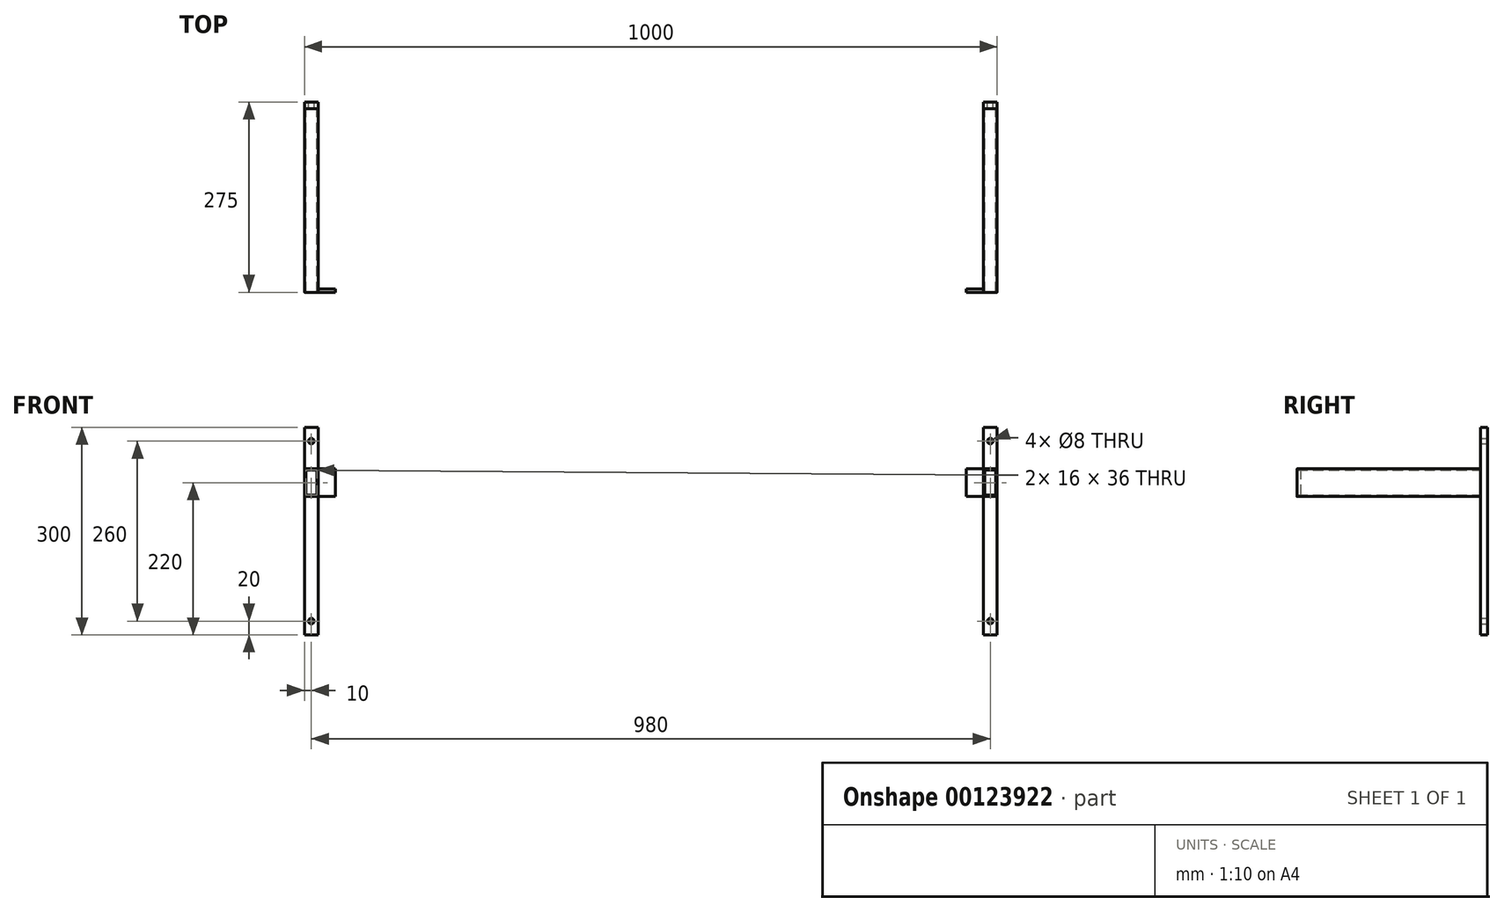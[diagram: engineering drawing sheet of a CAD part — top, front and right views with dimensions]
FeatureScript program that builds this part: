
annotation { "Feature Type Name" : "Feature", "Feature Type Description" : "" }
export const myFeature = defineFeature(function(context is Context, id is Id, definition is map)
    precondition{}
    {
        {
            var Q0;
            Q0=qCreatedBy(makeId("Front.planeOp"),FACE);
            var sketch = newSketch(context, id + "F0", { "sketchPlane" : qUnion([Q0])});
            skLineSegment(sketch, "E0.bottom", {"start": v(10, -150) * mm, "end": v(-10, -150) * mm});
            skLineSegment(sketch, "E0.top", {"start": v(10, 150) * mm, "end": v(-10, 150) * mm});
            skLineSegment(sketch, "E0.left", {"start": v(10, -150) * mm, "end": v(10, 150) * mm});
            skLineSegment(sketch, "E0.right", {"start": v(-10, -150) * mm, "end": v(-10, 150) * mm});
            skPoint(sketch, "E0.middle", {"position": v(0, 0) * mm});
            skLineSegment(sketch, "E1", {"start": v(0, 150) * mm, "end": v(0, -150) * mm, "construction": true});
            skCircle(sketch, "E2", {"center": v(0, 130) * mm, "radius": 4 * mm});
            skCircle(sketch, "E3", {"center": v(0, -130) * mm, "radius": 4 * mm});
            skSolve(sketch);
        }
        {
            var Q0;
            Q0 = qSketchRegion(id + "F0", true);
            extrude(context, id + "F1", {"entities" : qUnion([Q0]), "depth" : 10 * mm});
        }
        {
            var Q0;
            Q0=makeQuery(id+"F1.opExtrude","CAP_FACE",FACE,{"disambiguationData":[OSD([sQuery(id+"F0.wireOp",EDGE,"E0.bottom"),sQuery(id+"F0.wireOp",EDGE,"E0.top"),sQuery(id+"F0.wireOp",EDGE,"E0.left"),sQuery(id+"F0.wireOp",EDGE,"E0.right")])],"isStart":false});
            var sketch = newSketch(context, id + "F2", { "sketchPlane" : qUnion([Q0])});
            skLineSegment(sketch, "E4.bottom", {"start": v(-8, 90) * mm, "end": v(8, 90) * mm});
            skLineSegment(sketch, "E4.top", {"start": v(-8, 50) * mm, "end": v(8, 50) * mm});
            skLineSegment(sketch, "E4.left", {"start": v(-10, 88) * mm, "end": v(-10, 52) * mm});
            skLineSegment(sketch, "E4.right", {"start": v(10, 88) * mm, "end": v(10, 52) * mm});
            skPoint(sketch, "E5.visualSharp", {"position": v(-10, 90) * mm});
            skArc(sketch, "E5.filletArc", {"start": v(-8, 90) * mm, "mid": v(-9.41, 89.41) * mm, "end": v(-10, 88) * mm});
            skPoint(sketch, "E6.visualSharp", {"position": v(10, 90) * mm});
            skArc(sketch, "E6.filletArc", {"start": v(10, 88) * mm, "mid": v(9.41, 89.41) * mm, "end": v(8, 90) * mm});
            skPoint(sketch, "E7.visualSharp", {"position": v(10, 50) * mm});
            skArc(sketch, "E7.filletArc", {"start": v(8, 50) * mm, "mid": v(9.41, 50.59) * mm, "end": v(10, 52) * mm});
            skPoint(sketch, "E8.visualSharp", {"position": v(-10, 50) * mm});
            skArc(sketch, "E8.filletArc", {"start": v(-10, 52) * mm, "mid": v(-9.41, 50.59) * mm, "end": v(-8, 50) * mm});
            skLineSegment(sketch, "E9", {"start": v(0, 90) * mm, "end": v(0, 50) * mm});
            skLineSegment(sketch, "E10.bottom", {"start": v(8, 52) * mm, "end": v(-8, 52) * mm});
            skLineSegment(sketch, "E10.top", {"start": v(8, 88) * mm, "end": v(-8, 88) * mm});
            skLineSegment(sketch, "E10.left", {"start": v(8, 52) * mm, "end": v(8, 88) * mm});
            skLineSegment(sketch, "E10.right", {"start": v(-8, 52) * mm, "end": v(-8, 88) * mm});
            skPoint(sketch, "E10.middle", {"position": v(0, 70) * mm});
            skSolve(sketch);
        }
        {
            var Q0;
            Q0 = qSketchRegion(id + "F2", true);
            extrude(context, id + "F3", {"entities" : qUnion([Q0]), "depth" : (300 - 25 - 10) * mm});
        }
        {
            var Q0;
            Q0=qCreatedBy(makeId("Right.planeOp"),FACE);
            cPlane(context, id + "F4", {"entities" : qUnion([Q0]), "cplaneType" : CPlaneType.OFFSET, "offset" : 10 * mm, "oppositeDirection" : true, "width" : 150 * mm, "height" : 150 * mm});
        }
        {
            var Q0;
            Q0=qCreatedBy(id+"F4.planeOp",FACE);
            cPlane(context, id + "F5", {"entities" : qUnion([Q0]), "cplaneType" : CPlaneType.OFFSET, "offset" : 500 * mm, "width" : 150 * mm, "height" : 150 * mm});
        }
        {
            var Q0;
            Q0=makeQuery(id+"F3.boolean.opBoolean","MERGE",FACE,{"derivedFrom":[makeQuery(id+"F1.opExtrude","SWEPT_FACE",FACE,{"disambiguationData":[OSD([sQuery(id+"F0.wireOp",EDGE,"E0.left")])]}),makeQuery(id+"F3.opExtrude","SWEPT_FACE",FACE,{"disambiguationData":[OSD([sQuery(id+"F2.wireOp",EDGE,"E4.right")])]})]});
            var sketch = newSketch(context, id + "F6", { "sketchPlane" : qUnion([Q0])});
            skLineSegment(sketch, "E11", {"start": v(-275, 88) * mm, "end": v(-275, 52) * mm, "construction": true});
            skLineSegment(sketch, "E12.bottom", {"start": v(-275, 90) * mm, "end": v(-270, 90) * mm});
            skLineSegment(sketch, "E12.top", {"start": v(-275, 50) * mm, "end": v(-270, 50) * mm});
            skLineSegment(sketch, "E12.left", {"start": v(-275, 90) * mm, "end": v(-275, 50) * mm});
            skLineSegment(sketch, "E12.right", {"start": v(-270, 90) * mm, "end": v(-270, 50) * mm});
            skSolve(sketch);
        }
        {
            var Q0;
            Q0 = qSketchRegion(id + "F6", true);
            extrude(context, id + "F7", {"entities" : qUnion([Q0]), "depth" : 25 * mm});
        }
        {
            var Q0;
            Q0=makeQuery(id+"F1.opExtrude","SWEPT_BODY",BODY,{"disambiguationData":[OSD([sQuery(id+"F0.wireOp",EDGE,"E0.bottom"),sQuery(id+"F0.wireOp",EDGE,"E0.top"),sQuery(id+"F0.wireOp",EDGE,"E0.left"),sQuery(id+"F0.wireOp",EDGE,"E0.right")])]});
            var Q1;
            Q1=makeQuery(id+"F3.opExtrude","SWEPT_BODY",BODY,{"disambiguationData":[OSD([sQuery(id+"F2.wireOp",EDGE,"E4.bottom"),sQuery(id+"F2.wireOp",EDGE,"E4.top"),sQuery(id+"F2.wireOp",EDGE,"E4.left"),sQuery(id+"F2.wireOp",EDGE,"E4.right"),sQuery(id+"F2.wireOp",EDGE,"E5.filletArc"),sQuery(id+"F2.wireOp",EDGE,"E6.filletArc"),sQuery(id+"F2.wireOp",EDGE,"E7.filletArc"),sQuery(id+"F2.wireOp",EDGE,"E8.filletArc"),sQuery(id+"F2.wireOp",EDGE,"E10.bottom"),sQuery(id+"F2.wireOp",EDGE,"E10.top"),sQuery(id+"F2.wireOp",EDGE,"E10.left"),sQuery(id+"F2.wireOp",EDGE,"E10.right")])]});
            var Q2;
            Q2=makeQuery(id+"F7.opExtrude","SWEPT_BODY",BODY,{"disambiguationData":[OSD([sQuery(id+"F6.wireOp",EDGE,"E12.bottom"),sQuery(id+"F6.wireOp",EDGE,"E12.top"),sQuery(id+"F6.wireOp",EDGE,"E12.left"),sQuery(id+"F6.wireOp",EDGE,"E12.right")])]});
            var Q3;
            Q3=qCreatedBy(id+"F5.planeOp",FACE);
            mirror(context, id + "F8", {"entities" : qUnion([Q0, Q1, Q2]), "mirrorPlane" : qUnion([Q3])});
        }
    });
